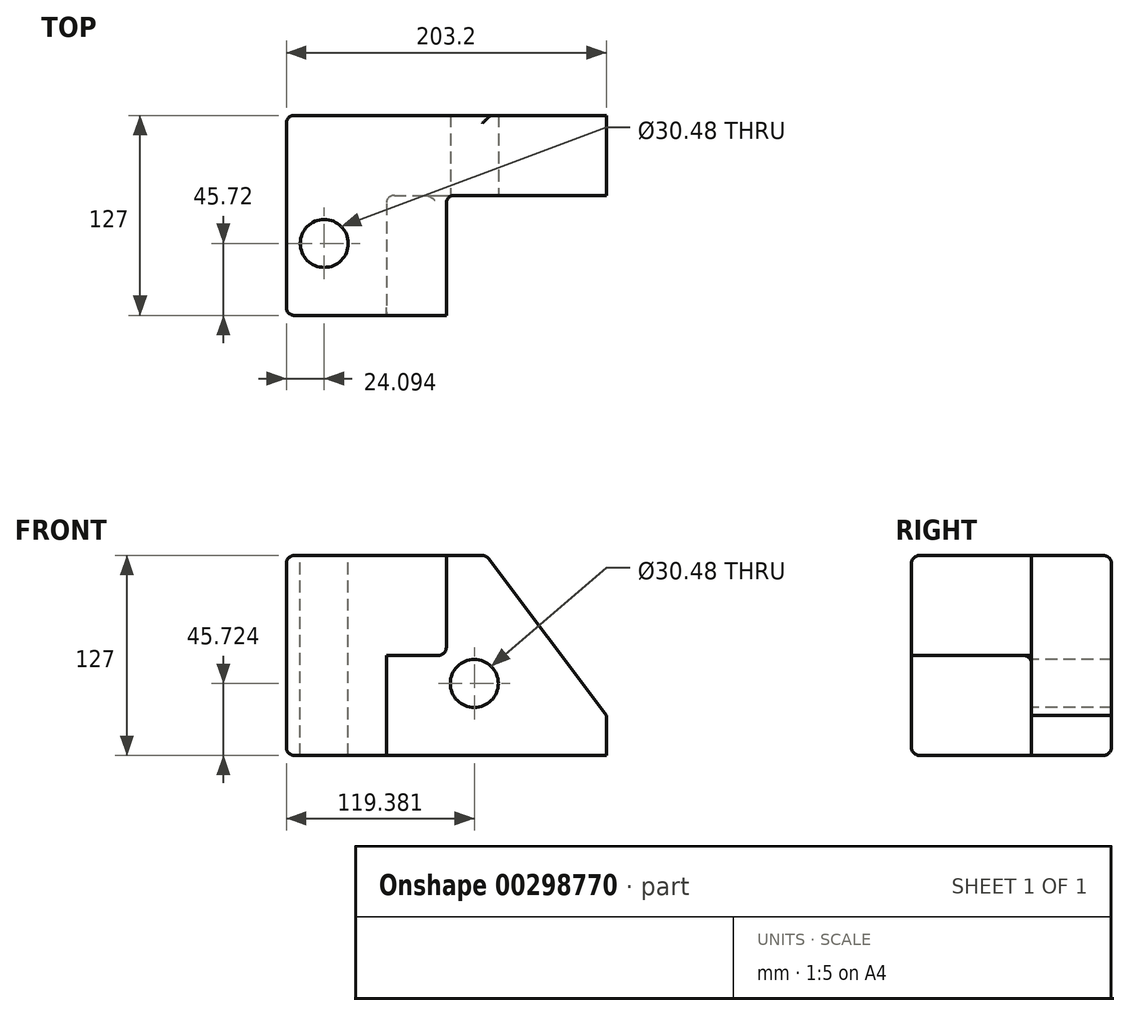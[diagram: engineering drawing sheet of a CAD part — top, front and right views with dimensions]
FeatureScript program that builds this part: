
annotation { "Feature Type Name" : "Feature", "Feature Type Description" : "" }
export const myFeature = defineFeature(function(context is Context, id is Id, definition is map)
    precondition{}
    {
        {
            var Q0;
            Q0=qCreatedBy(makeId("Front.planeOp"),FACE);
            var sketch = newSketch(context, id + "F0", { "sketchPlane" : qUnion([Q0])});
            skLineSegment(sketch, "E0.bottom", {"start": v(-98.8, 75.43) * mm, "end": v(104.4, 75.43) * mm});
            skLineSegment(sketch, "E0.top", {"start": v(-98.8, -51.57) * mm, "end": v(104.4, -51.57) * mm});
            skLineSegment(sketch, "E0.left", {"start": v(-98.8, 75.43) * mm, "end": v(-98.8, -51.57) * mm});
            skLineSegment(sketch, "E0.right", {"start": v(104.4, 75.43) * mm, "end": v(104.4, -51.57) * mm});
            skSolve(sketch);
        }
        {
            var Q0;
            Q0=makeQuery(id+"F0.imprint","IMPRINT",FACE,{"disambiguationData":[TD([[makeQuery(id+"F0.imprint","IMPRINT",EDGE,{"derivedFrom":sQuery(id+"F0.wireOp",EDGE,"E0.bottom")}),-1.0]])]});
            extrude(context, id + "F1", {"entities" : qUnion([Q0]), "depth" : 127 * mm});
        }
        {
            var Q0;
            Q0=makeQuery(id+"F1.opExtrude","CAP_FACE",FACE,{"disambiguationData":[OSD([sQuery(id+"F0.wireOp",EDGE,"E0.bottom"),sQuery(id+"F0.wireOp",EDGE,"E0.top"),sQuery(id+"F0.wireOp",EDGE,"E0.left"),sQuery(id+"F0.wireOp",EDGE,"E0.right")])],"isStart":false});
            var sketch = newSketch(context, id + "F2", { "sketchPlane" : qUnion([Q0])});
            skLineSegment(sketch, "E1", {"start": v(-98.8, -51.57) * mm, "end": v(-35.3, -51.57) * mm});
            skLineSegment(sketch, "E2", {"start": v(-35.3, -51.57) * mm, "end": v(-35.3, 11.93) * mm});
            skLineSegment(sketch, "E3", {"start": v(-35.3, 11.93) * mm, "end": v(2.8, 11.93) * mm});
            skLineSegment(sketch, "E4", {"start": v(-98.8, -51.57) * mm, "end": v(-98.8, 75.43) * mm});
            skLineSegment(sketch, "E5", {"start": v(-98.8, 75.43) * mm, "end": v(2.8, 75.43) * mm});
            skLineSegment(sketch, "E6", {"start": v(2.8, 75.43) * mm, "end": v(2.8, 11.93) * mm});
            skSolve(sketch);
        }
        {
            var Q0;
            {var subQ3=sQuery(id+"F2.wireOp",EDGE,"E2");Q0=makeQuery(id+"F2.imprint","IMPRINT",FACE,{"disambiguationData":[TD([[makeQuery(id+"F2.imprint","IMPRINT",EDGE,{"derivedFrom":subQ3}),-1.0]])]});}
            extrude(context, id + "F3", {"entities" : qUnion([Q0]), "operationType" : NewBodyOperationType.REMOVE, "oppositeDirection" : true, "depth" : 76.2 * mm});
        }
        {
            var Q0;
            Q0=makeQuery(id+"F1.opExtrude","SWEPT_EDGE",EDGE,{"disambiguationData":[OSD([sQuery(id+"F0.wireOp",EDGE,"E0.bottom"),sQuery(id+"F0.wireOp",EDGE,"E0.right")])]});
            chamfer(context, id + "F4", {"entities" : qUnion([Q0]), "chamferType" : ChamferType.TWO_OFFSETS, "width1" : 76.2 * mm, "oppositeDirection" : false, "width2" : 101.6 * mm, "tangentPropagation" : true});
        }
        {
            var Q0;
            Q0=makeQuery(id+"F1.opExtrude","CAP_EDGE",EDGE,{"disambiguationData":[OSD([sQuery(id+"F0.wireOp",EDGE,"E0.bottom")])],"isStart":false});
            var Q1;
            Q1=makeQuery(id+"F1.opExtrude","SWEPT_EDGE",EDGE,{"disambiguationData":[OSD([sQuery(id+"F0.wireOp",EDGE,"E0.bottom"),sQuery(id+"F0.wireOp",EDGE,"E0.left")])]});
            var Q2;
            Q2=makeQuery(id+"F1.opExtrude","CAP_EDGE",EDGE,{"disambiguationData":[OSD([sQuery(id+"F0.wireOp",EDGE,"E0.bottom")])],"isStart":true});
            var Q3;
            Q3=makeQuery(id+"F3.boolean.opBoolean","COPY",EDGE,{"derivedFrom":makeQuery(id+"F3.opExtrude","SWEPT_EDGE",EDGE,{"disambiguationData":[OSD([sQuery(id+"F0.wireOp",EDGE,"E0.bottom"),sQuery(id+"F2.wireOp",EDGE,"E5"),sQuery(id+"F2.wireOp",EDGE,"E6")])]})});
            var Q4;
            Q4=makeQuery(id+"F3.boolean.opBoolean","COPY",EDGE,{"derivedFrom":makeQuery(id+"F3.opExtrude","CAP_EDGE",EDGE,{"disambiguationData":[OSD([sQuery(id+"F0.wireOp",EDGE,"E0.bottom")])],"isStart":false})});
            var Q5;
            Q5=makeQuery(id+"F3.boolean.opBoolean","COPY",EDGE,{"derivedFrom":makeQuery(id+"F3.opExtrude","CAP_EDGE",EDGE,{"disambiguationData":[OSD([sQuery(id+"F2.wireOp",EDGE,"E6")])],"isStart":false})});
            var Q6;
            Q6=makeQuery(id+"F3.boolean.opBoolean","COPY",EDGE,{"derivedFrom":makeQuery(id+"F3.opExtrude","CAP_EDGE",EDGE,{"disambiguationData":[OSD([sQuery(id+"F2.wireOp",EDGE,"E6")])],"isStart":true})});
            var Q7;
            Q7=makeQuery(id+"F3.boolean.opBoolean","COPY",EDGE,{"derivedFrom":makeQuery(id+"F3.opExtrude","SWEPT_EDGE",EDGE,{"disambiguationData":[OSD([sQuery(id+"F2.wireOp",EDGE,"E3"),sQuery(id+"F2.wireOp",EDGE,"E6")])]})});
            var Q8;
            Q8=makeQuery(id+"F3.boolean.opBoolean","COPY",EDGE,{"derivedFrom":makeQuery(id+"F3.opExtrude","CAP_EDGE",EDGE,{"disambiguationData":[OSD([sQuery(id+"F2.wireOp",EDGE,"E2")])],"isStart":false})});
            var Q9;
            Q9=makeQuery(id+"F3.boolean.opBoolean","COPY",EDGE,{"derivedFrom":makeQuery(id+"F3.opExtrude","CAP_EDGE",EDGE,{"disambiguationData":[OSD([sQuery(id+"F0.wireOp",EDGE,"E0.top")])],"isStart":false})});
            var Q10;
            Q10=makeQuery(id+"F3.boolean.opBoolean","COPY",EDGE,{"derivedFrom":makeQuery(id+"F3.opExtrude","SWEPT_EDGE",EDGE,{"disambiguationData":[OSD([sQuery(id+"F0.wireOp",EDGE,"E0.top"),sQuery(id+"F2.wireOp",EDGE,"E1"),sQuery(id+"F2.wireOp",EDGE,"E2")])]})});
            var Q11;
            Q11=makeQuery(id+"F3.boolean.opBoolean","COPY",EDGE,{"derivedFrom":makeQuery(id+"F3.opExtrude","CAP_EDGE",EDGE,{"disambiguationData":[OSD([sQuery(id+"F2.wireOp",EDGE,"E2")])],"isStart":true})});
            var Q12;
            Q12=makeQuery(id+"F1.opExtrude","CAP_EDGE",EDGE,{"disambiguationData":[OSD([sQuery(id+"F0.wireOp",EDGE,"E0.top")])],"isStart":false});
            var Q13;
            Q13=makeQuery(id+"F1.opExtrude","CAP_EDGE",EDGE,{"disambiguationData":[OSD([sQuery(id+"F0.wireOp",EDGE,"E0.left")])],"isStart":false});
            var Q14;
            Q14=makeQuery(id+"F1.opExtrude","CAP_EDGE",EDGE,{"disambiguationData":[OSD([sQuery(id+"F0.wireOp",EDGE,"E0.top")])],"isStart":true});
            var Q15;
            Q15=makeQuery(id+"F1.opExtrude","CAP_EDGE",EDGE,{"disambiguationData":[OSD([sQuery(id+"F0.wireOp",EDGE,"E0.left")])],"isStart":true});
            var Q16;
            Q16=makeQuery(id+"F1.opExtrude","SWEPT_EDGE",EDGE,{"disambiguationData":[OSD([sQuery(id+"F0.wireOp",EDGE,"E0.top"),sQuery(id+"F0.wireOp",EDGE,"E0.left")])]});
            var Q17;
            {var subQ0=sQuery(id+"F0.wireOp",EDGE,"E0.bottom");Q17=makeQuery(id+"F4.opChamfer","BLEND_EDGE",EDGE,{"blendedFrom":[makeQuery(id+"F1.opExtrude","SWEPT_EDGE",EDGE,{"disambiguationData":[OSD([subQ0,sQuery(id+"F0.wireOp",EDGE,"E0.right")])]}),makeQuery(id+"F1.opExtrude","SWEPT_FACE",FACE,{"disambiguationData":[OSD([subQ0])]})],"blendedInto":[makeQuery(id+"F1.opExtrude","SWEPT_FACE",FACE,{"disambiguationData":[OSD([subQ0])]})]});}
            var Q18;
            Q18=makeQuery(id+"F3.boolean.opBoolean","COPY",EDGE,{"derivedFrom":makeQuery(id+"F3.opExtrude","CAP_EDGE",EDGE,{"disambiguationData":[OSD([sQuery(id+"F2.wireOp",EDGE,"E3")])],"isStart":true})});
            fillet(context, id + "F5", {"entities" : qUnion([Q0, Q1, Q2, Q3, Q4, Q5, Q6, Q7, Q8, Q9, Q10, Q11, Q12, Q13, Q14, Q15, Q16, Q17, Q18]), "radius" : 5.08 * mm, "tangentPropagation" : true, "allowEdgeOverflow" : false});
        }
        {
            var Q0;
            Q0=makeQuery(id+"F3.boolean.opBoolean","COPY",FACE,{"derivedFrom":makeQuery(id+"F3.opExtrude","CAP_FACE",FACE,{"disambiguationData":[OSD([sQuery(id+"F0.wireOp",EDGE,"E0.bottom"),sQuery(id+"F0.wireOp",EDGE,"E0.top"),sQuery(id+"F0.wireOp",EDGE,"E0.right"),sQuery(id+"F2.wireOp",EDGE,"E2"),sQuery(id+"F2.wireOp",EDGE,"E3"),sQuery(id+"F2.wireOp",EDGE,"E6")])],"isStart":false})});
            var sketch = newSketch(context, id + "F6", { "sketchPlane" : qUnion([Q0])});
            skCircle(sketch, "E7", {"center": v(20.58, -5.85) * mm, "radius": 15.24 * mm});
            skSolve(sketch);
        }
        {
            var Q0;
            Q0=makeQuery(id+"F6.imprint","IMPRINT",FACE,{"disambiguationData":[TD([[makeQuery(id+"F6.imprint","IMPRINT",EDGE,{"derivedFrom":sQuery(id+"F6.wireOp",EDGE,"E7")}),1.0]])]});
            var Q1;
            Q1=sQuery(id+"F6.wireOp",EDGE,"E7");
            extrude(context, id + "F7", {"entities" : qUnion([Q0]), "operationType" : NewBodyOperationType.REMOVE, "surfaceEntities" : qUnion([Q1]), "endBound" : BoundingType.THROUGH_ALL, "oppositeDirection" : true, "depth" : 25.4 * mm});
        }
        {
            var Q0;
            Q0=makeQuery(id+"F1.opExtrude","SWEPT_FACE",FACE,{"disambiguationData":[OSD([sQuery(id+"F0.wireOp",EDGE,"E0.bottom")])]});
            var sketch = newSketch(context, id + "F8", { "sketchPlane" : qUnion([Q0])});
            skCircle(sketch, "E8", {"center": v(-74.7, -81.28) * mm, "radius": 15.24 * mm});
            skSolve(sketch);
        }
        {
            var Q0;
            Q0=makeQuery(id+"F8.imprint","IMPRINT",FACE,{"disambiguationData":[TD([[makeQuery(id+"F8.imprint","IMPRINT",EDGE,{"derivedFrom":sQuery(id+"F8.wireOp",EDGE,"E8")}),1.0]])]});
            var sketch = newSketch(context, id + "F9", { "sketchPlane" : qUnion([Q0])});
            skSolve(sketch);
        }
        {
            var Q0;
            Q0 = qSketchRegion(id + "F9", true);
            var Q1;
            Q1=makeQuery(id+"F8.imprint","IMPRINT",FACE,{"disambiguationData":[TD([[makeQuery(id+"F8.imprint","IMPRINT",EDGE,{"derivedFrom":sQuery(id+"F8.wireOp",EDGE,"E8")}),1.0]])]});
            extrude(context, id + "F10", {"entities" : qUnion([Q0, Q1]), "operationType" : NewBodyOperationType.REMOVE, "endBound" : BoundingType.THROUGH_ALL, "oppositeDirection" : true, "depth" : 25.4 * mm});
        }
    });
